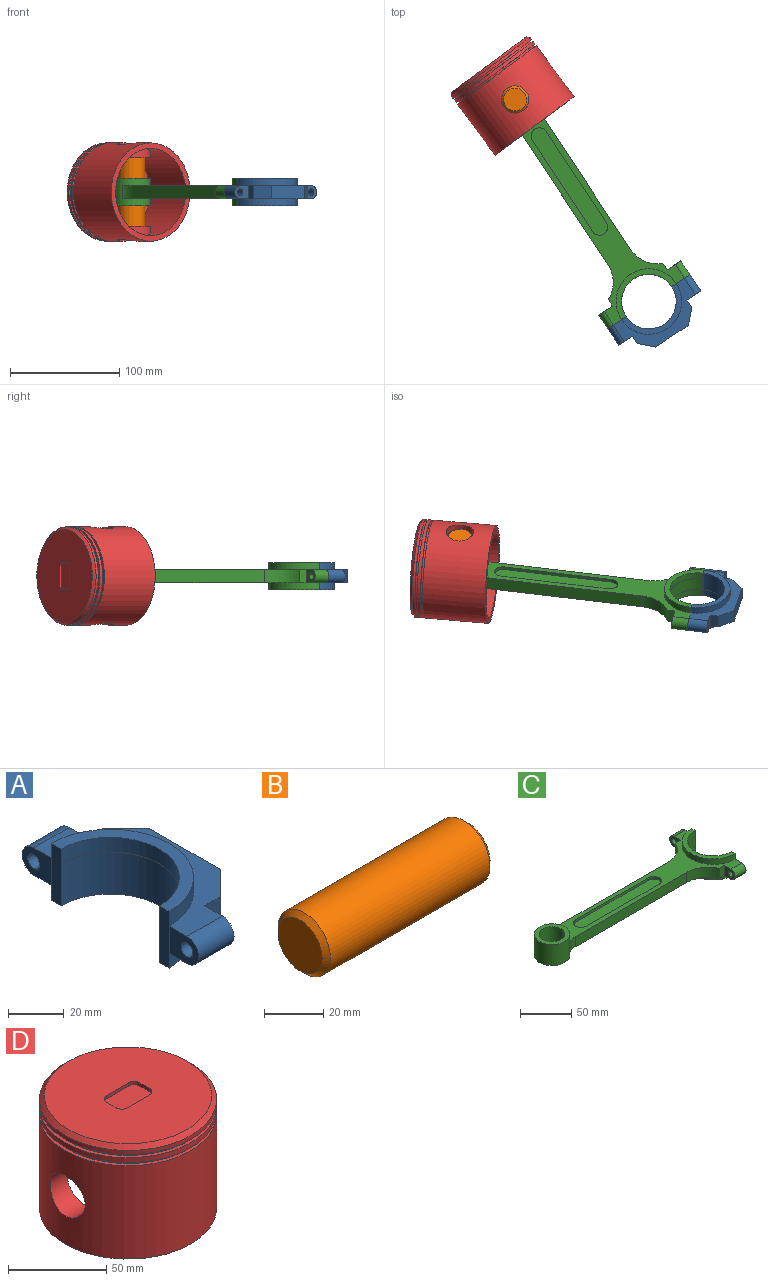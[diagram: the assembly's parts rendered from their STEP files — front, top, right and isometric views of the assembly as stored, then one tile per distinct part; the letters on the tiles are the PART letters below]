
ASSEMBLY  parts=4 mates=6
PART A: 23 faces, bbox 38.1x90x25 mm
  f0: plane 15x12mm, normal (-1,0,0), area 136.3mm2, adj f7,f8,f9,f16,f22
  f1: plane 15x12mm, normal (-1,0,0), area 136.3mm2, adj f7,f8,f11,f16,f21
  f2: plane 12x8mm, normal (0,1,0), area 96mm2, adj f6,f7,f8,f12
  f3: plane 12x8mm, normal (0,-1,0), area 96mm2, adj f4,f7,f8,f10
  f4: plane 12x12mm, normal (0.71,-0.71,0), area 203.6mm2, adj f3,f5,f7,f8
  f5: plane 36x12mm, normal (1,0,0), area 432mm2, adj f4,f6,f7,f8
  f6: plane 12x12mm, normal (0.71,0.71,0), area 203.6mm2, adj f2,f5,f7,f8
  f7: plane 78x38mm, normal (0,0,1), area 1050.2mm2, adj f0,f1,f2,f3,f4,f5,f6,f9
  f8: plane 78x38mm, normal (0,0,-1), area 1050.2mm2, adj f0,f1,f2,f3,f4,f5,f6,f9
  f9: cylinder r=6mm len=18mm, axis (-1,0,0), area 339.3mm2, adj f0,f7,f8,f10
  f10: plane 15x12mm, normal (1,0,0), area 136.3mm2, adj f3,f7,f8,f9,f22
  f11: cylinder r=6mm len=18mm, axis (-1,0,0), area 339.3mm2, adj f1,f7,f8,f12
  f12: plane 15x12mm, normal (1,0,0), area 136.3mm2, adj f2,f7,f8,f11,f21
  f13: plane 25x5mm, normal (-1,0,0), area 125mm2, adj f14,f16,f17,f18
  f14: cylinder r=25mm len=50mm, axis (0,0,-1), area 512.9mm2, adj f13,f15,f17,f18,f19,f20
  f15: plane 25x5mm, normal (-1,0,0), area 125mm2, adj f14,f16,f17,f18
  f16: cylinder r=30mm len=60mm, axis (0,0,-1), area 1226.8mm2, adj f0,f1,f7,f8,f13,f15,f17,f18
  f17: plane 60x30mm, normal (0,0,1), area 432mm2, adj f13,f14,f15,f16
  f18: plane 60x30mm, normal (0,0,-1), area 428.7mm2, adj f13,f14,f15,f16,f20
  f19: plane 50x25mm, normal (0,0,-1), area 3.3mm2, adj f14,f20
  f20: cylinder r=25mm len=50mm, axis (0,0,1), area 1453mm2, adj f14,f18,f19
  f21: cylinder r=3mm len=18mm, axis (-1,0,0), area 339.3mm2, adj f1,f12
  f22: cylinder r=3mm len=18mm, axis (-1,0,0), area 339.3mm2, adj f0,f10
PART B: 5 faces, bbox 80x25x25 mm
  f0: cylinder r=12.5mm len=76mm, axis (-1,0,0), area 5969mm2, adj f3,f4
  f1: plane 21x21mm, normal (1,0,0), area 346.4mm2, adj f4
  f2: plane 21x21mm, normal (-1,0,0), area 346.4mm2, adj f3
  f3: cone r=12.5mm half-angle=45deg, axis (1,0,0), area 204.4mm2, adj f0,f2
  f4: cone r=10.5mm half-angle=45deg, axis (-1,0,0), area 204.4mm2, adj f0,f1
PART C: 44 faces, bbox 239.6x90x25 mm
  f0: plane 213.48x78mm, normal (0,0,1), area 3369.8mm2, adj f2,f3,f4,f5,f6,f9,f10,f12
  f1: cylinder r=25mm len=50mm, axis (0,0,-1), area 512.6mm2, adj f19,f21,f28
  f2: plane 12x7mm, normal (0,-1,0), area 84mm2, adj f0,f11,f12,f24
  f3: plane 12x7mm, normal (0,1,0), area 84mm2, adj f0,f11,f13,f23
  f4: plane 15x12mm, normal (1,0,0), area 136.3mm2, adj f0,f11,f15,f25,f30
  f5: plane 15x12mm, normal (1,0,0), area 136.3mm2, adj f0,f11,f15,f22,f31
  f6: cylinder r=17.5mm len=35mm, axis (0,0,-1), area 2302.8mm2, adj f0,f7,f8,f11,f32,f33
  f7: plane 35x35mm, normal (0,0,1), area 471.2mm2, adj f6,f26
  f8: plane 35x35mm, normal (0,0,-1), area 471.2mm2, adj f6,f26
  f9: plane 153.49x12mm, normal (0,1,0), area 1841.9mm2, adj f0,f11,f13,f32
  f10: plane 153.49x12mm, normal (0,-1,0), area 1841.9mm2, adj f0,f11,f12,f33
  f11: plane 213.48x78mm, normal (0,0,-1), area 3369.8mm2, adj f2,f3,f4,f5,f6,f9,f10,f12
  f12: cylinder r=30mm len=27.27mm, axis (0,0,1), area 410.8mm2, adj f0,f2,f10,f11
  f13: cylinder r=30mm len=27.27mm, axis (0,0,1), area 410.8mm2, adj f0,f3,f9,f11
  f14: plane 25x5mm, normal (1,0,0), area 125mm2, adj f15,f17,f18,f19,f27,f28
  f15: cylinder r=30mm len=60mm, axis (0,0,-1), area 1235.6mm2, adj f0,f4,f5,f11,f14,f16,f18,f19
  f16: plane 25x5mm, normal (1,0,0), area 125mm2, adj f15,f17,f18,f19,f28,f29
  f17: cylinder r=25mm len=50mm, axis (0,0,-1), area 514.2mm2, adj f14,f16,f18,f20,f27,f29
  f18: plane 60x30.28mm, normal (0,0,1), area 434.8mm2, adj f14,f15,f16,f17
  f19: plane 60x30.28mm, normal (0,0,-1), area 434.8mm2, adj f1,f14,f15,f16,f28
  f20: plane 50x25.16mm, normal (0,0,1), area 8mm2, adj f17,f28
  f21: plane 50x25.16mm, normal (0,0,-1), area 8mm2, adj f1,f28
  f22: cylinder r=6mm len=15mm, axis (1,0,0), area 282.7mm2, adj f0,f5,f11,f23
  f23: plane 15x12mm, normal (-1,0,0), area 136.3mm2, adj f0,f3,f11,f22,f31
  f24: plane 15x12mm, normal (-1,0,0), area 136.3mm2, adj f0,f2,f11,f25,f30
  f25: cylinder r=6mm len=15mm, axis (1,0,0), area 282.7mm2, adj f0,f4,f11,f24
  f26: cylinder r=12.5mm len=25mm, axis (0,0,1), area 1963.5mm2, adj f7,f8
  f27: plane 0.13x0mm, normal (0,0,-1), area 0mm2, adj f14,f17,f28
  f28: cylinder r=25mm len=50mm, axis (0,0,1), area 947.1mm2, adj f1,f14,f16,f19,f20,f21,f27,f29
  f29: plane 0.13x0mm, normal (0,0,-1), area 0mm2, adj f16,f17,f28
  f30: cylinder r=3mm len=15mm, axis (1,0,0), area 282.7mm2, adj f4,f24
  f31: cylinder r=3mm len=15mm, axis (1,0,0), area 282.7mm2, adj f5,f23
  f32: cylinder r=22mm len=12mm, axis (0,0,-1), area 134.3mm2, adj f0,f6,f9,f11
  f33: cylinder r=22mm len=12mm, axis (0,0,-1), area 134.3mm2, adj f0,f6,f10,f11
  f34: plane 100x3mm, normal (0,-1,0), area 300mm2, adj f0,f35,f37,f38
  f35: cylinder r=7.5mm len=15mm, axis (0,0,1), area 70.7mm2, adj f0,f34,f36,f38
  f36: plane 100x3mm, normal (0,1,0), area 300mm2, adj f0,f35,f37,f38
  f37: cylinder r=7.5mm len=15mm, axis (0,0,1), area 70.7mm2, adj f0,f34,f36,f38
  f38: plane 115x15mm, normal (0,0,1), area 1676.7mm2, adj f34,f35,f36,f37
  f39: cylinder r=7.5mm len=15mm, axis (0,0,-1), area 70.7mm2, adj f11,f40,f42,f43
  f40: plane 100x3mm, normal (0,-1,0), area 300mm2, adj f11,f39,f41,f43
  f41: cylinder r=7.5mm len=15mm, axis (0,0,-1), area 70.7mm2, adj f11,f40,f42,f43
  f42: plane 100x3mm, normal (0,1,0), area 300mm2, adj f11,f39,f41,f43
  f43: plane 115x15mm, normal (0,0,-1), area 1676.7mm2, adj f39,f40,f41,f42
PART D: 29 faces, bbox 90x90x70 mm
  f0: plane 85x85mm, normal (0,0,1), area 5328.2mm2, adj f19,f20,f21,f22,f23,f25,f26,f27
  f1: cylinder r=45mm len=90mm, axis (0,0,-1), area 706.9mm2, adj f2,f19
  f2: plane 90x90mm, normal (0,0,-1), area 552.9mm2, adj f1,f3
  f3: cylinder r=43mm len=86mm, axis (0,0,-1), area 540.4mm2, adj f2,f4
  f4: plane 90x90mm, normal (0,0,1), area 552.9mm2, adj f3,f5
  f5: cylinder r=45mm len=90mm, axis (0,0,-1), area 848.2mm2, adj f4,f6
  f6: plane 90x90mm, normal (0,0,-1), area 552.9mm2, adj f5,f7
  f7: cylinder r=43mm len=86mm, axis (0,0,-1), area 540.4mm2, adj f6,f8
  f8: plane 90x90mm, normal (0,0,1), area 552.9mm2, adj f7,f9
  f9: cylinder r=45mm len=90mm, axis (0,0,-1), area 15407.2mm2, adj f8,f10,f17,f18
  f10: plane 90x90mm, normal (0,0,-1), area 1335.2mm2, adj f9,f11
  f11: cylinder r=40mm len=80mm, axis (0,0,-1), area 11849.8mm2, adj f10,f12,f13,f15
  f12: plane 80x80mm, normal (0,0,-1), area 5026.5mm2, adj f11
  f13: cylinder r=17.5mm len=35mm, axis (-1,0,0), area 753.4mm2, adj f11,f14
  f14: plane 35x35mm, normal (1,0,0), area 471.2mm2, adj f13,f18
  f15: cylinder r=17.5mm len=35mm, axis (-1,0,0), area 749.5mm2, adj f11,f16
  f16: plane 35x35mm, normal (-1,0,0), area 471.2mm2, adj f15,f17
  f17: cylinder r=12.5mm len=25mm, axis (1,0,0), area 1015.3mm2, adj f9,f16
  f18: cylinder r=12.5mm len=25mm, axis (1,0,0), area 1017.8mm2, adj f9,f14
  f19: cone r=45mm half-angle=45deg, axis (0,0,-1), area 971.9mm2, adj f0,f1
  f20: plane 16x2mm, normal (0,1,0), area 32mm2, adj f0,f24,f25,f28
  f21: plane 7x2mm, normal (-1,0,0), area 14mm2, adj f0,f24,f25,f26
  f22: plane 16x2mm, normal (0,-1,0), area 32mm2, adj f0,f24,f26,f27
  f23: plane 7x2mm, normal (1,0,0), area 14mm2, adj f0,f24,f27,f28
  f24: plane 24x15mm, normal (0,0,1), area 346.3mm2, adj f20,f21,f22,f23,f25,f26,f27,f28
  f25: cylinder r=4mm len=4mm, axis (0,0,1), area 12.6mm2, adj f0,f20,f21,f24
  f26: cylinder r=4mm len=4mm, axis (0,0,-1), area 12.6mm2, adj f0,f21,f22,f24
  f27: cylinder r=4mm len=4mm, axis (0,0,1), area 12.6mm2, adj f0,f22,f23,f24
  f28: cylinder r=4mm len=4mm, axis (0,0,-1), area 12.6mm2, adj f0,f20,f23,f24
PLACE A rot(axis=(0.88,-0.47,0),180deg) t=(119.95,-14.44,-297.54)mm
PLACE B rot(axis=(-0.35,0.87,0.35),98deg) t=(-13.07,186.52,-297.22)mm
PLACE C rot(axis=(-0.88,0.47,0),180deg) t=(-13.07,186.52,-297.54)mm
PLACE D rot(axis=(-0.67,0.33,0.67),143deg) t=(4.84,162.46,-297.35)mm
MATE cylindrical B.f0 <-> D.f13  axis (0,0,1) through (-13.07,186.52,-257.22)mm
MATE slider C.f30 <-> A.f9  axis (0.55,-0.83,0) through (141.99,22.93,-297.54)mm
MATE cylindrical C.f26 <-> D.f13  axis (0,0,-1) through (-13.07,186.52,-310.04)mm
MATE planar B.f0 <-> D.f13  axis (0,0,1) through (-13.07,186.52,-257.22)mm
MATE planar C.f6 <-> D.f13  axis (0,0,-1) through (-13.07,186.52,-310.04)mm
MATE pin_slot C.f5 <-> A.f1  axis (0.55,-0.83,0) through (79.04,-18.74,-297.54)mm
